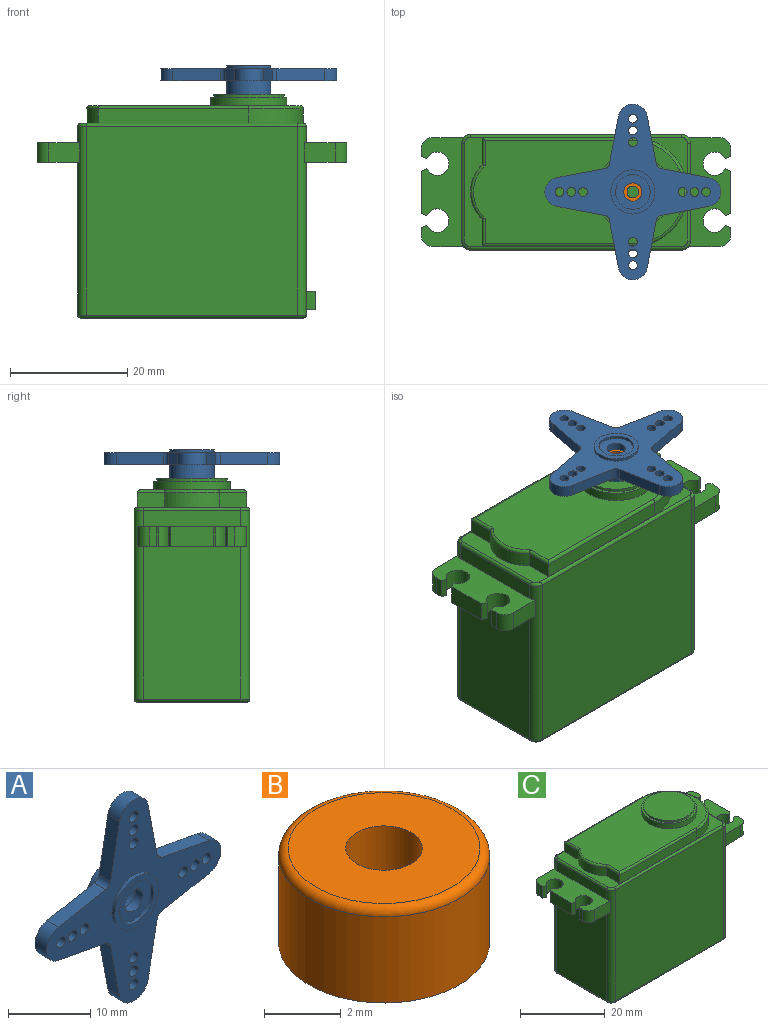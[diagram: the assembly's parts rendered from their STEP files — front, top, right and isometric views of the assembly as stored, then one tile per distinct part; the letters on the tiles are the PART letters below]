
ASSEMBLY  parts=3 mates=2
PART A: 39 faces, bbox 30x4.9x30 mm
  f0: plane 8.17x2mm, normal (-0.18,0,0.98), area 16.6mm2, adj f1,f24,f25,f38
  f1: cylinder r=2.5mm len=4.91mm, axis (0,1,0), area 13.8mm2, adj f0,f2,f24,f25
  f2: plane 8.17x2mm, normal (-0.18,0,-0.98), area 16.6mm2, adj f1,f24,f25,f35
  f3: plane 8.17x2mm, normal (-0.98,0,-0.18), area 16.6mm2, adj f4,f24,f25,f35
  f4: cylinder r=2.5mm len=4.91mm, axis (0,1,0), area 13.8mm2, adj f3,f5,f24,f25
  f5: plane 8.17x2mm, normal (0.98,0,-0.18), area 16.6mm2, adj f4,f24,f25,f36
  f6: plane 8.17x2mm, normal (0.18,0,-0.98), area 16.6mm2, adj f7,f24,f25,f36
  f7: cylinder r=2.5mm len=4.91mm, axis (0,1,0), area 13.8mm2, adj f6,f8,f24,f25
  f8: plane 8.17x2mm, normal (0.18,0,0.98), area 16.6mm2, adj f7,f24,f25,f37
  f9: plane 8.17x2mm, normal (0.98,0,0.18), area 16.6mm2, adj f10,f24,f25,f37
  f10: cylinder r=2.5mm len=4.91mm, axis (0,1,0), area 13.8mm2, adj f9,f23,f24,f25
  f11: cylinder r=0.75mm len=2mm, axis (0,1,0), area 9.4mm2, adj f24,f25
  f12: cylinder r=0.75mm len=2mm, axis (0,1,0), area 9.4mm2, adj f24,f25
  f13: cylinder r=0.75mm len=2mm, axis (0,1,0), area 9.4mm2, adj f24,f25
  f14: cylinder r=0.75mm len=2mm, axis (0,1,0), area 9.4mm2, adj f24,f25
  f15: cylinder r=0.75mm len=2mm, axis (0,1,0), area 9.4mm2, adj f24,f25
  f16: cylinder r=0.75mm len=2mm, axis (0,1,0), area 9.4mm2, adj f24,f25
  f17: cylinder r=0.75mm len=2mm, axis (0,1,0), area 9.4mm2, adj f24,f25
  f18: cylinder r=0.75mm len=2mm, axis (0,1,0), area 9.4mm2, adj f24,f25
  f19: cylinder r=0.75mm len=2mm, axis (0,1,0), area 9.4mm2, adj f24,f25
  f20: cylinder r=0.75mm len=2mm, axis (0,1,0), area 9.4mm2, adj f24,f25
  f21: cylinder r=0.75mm len=2mm, axis (0,1,0), area 9.4mm2, adj f24,f25
  f22: cylinder r=0.75mm len=2mm, axis (0,1,0), area 9.4mm2, adj f24,f25
  f23: plane 8.17x2mm, normal (-0.98,0,0.18), area 16.6mm2, adj f10,f24,f25,f38
  f24: plane 30x30mm, normal (0,-1,0), area 265.3mm2, adj f0,f1,f2,f3,f4,f5,f6,f7
  f25: plane 30x30mm, normal (0,1,0), area 265.3mm2, adj f0,f1,f2,f3,f4,f5,f6,f7
  f26: cylinder r=3.76mm len=7.52mm, axis (0,1,0), area 11.8mm2, adj f24,f27
  f27: plane 7.52x7.52mm, normal (0,-1,0), area 17.1mm2, adj f26,f32
  f28: cylinder r=3.76mm len=7.52mm, axis (0,-1,0), area 56.7mm2, adj f25,f29
  f29: plane 7.52x7.52mm, normal (0,1,0), area 17.1mm2, adj f28,f30
  f30: cylinder r=2.95mm len=5.9mm, axis (0,1,0), area 57.5mm2, adj f29,f31
  f31: plane 5.9x5.9mm, normal (0,1,0), area 19.8mm2, adj f30,f34
  f32: cylinder r=2.95mm len=5.9mm, axis (0,-1,0), area 9.3mm2, adj f27,f33
  f33: plane 5.9x5.9mm, normal (0,-1,0), area 19.8mm2, adj f32,f34
  f34: cylinder r=1.55mm len=3.1mm, axis (0,-1,0), area 12.7mm2, adj f31,f33
  f35: cylinder r=1mm len=2mm, axis (0,1,0), area 2.4mm2, adj f2,f3,f24,f25
  f36: cylinder r=1mm len=2mm, axis (0,1,0), area 2.4mm2, adj f5,f6,f24,f25
  f37: cylinder r=1mm len=2mm, axis (0,1,0), area 2.4mm2, adj f8,f9,f24,f25
  f38: cylinder r=1mm len=2mm, axis (0,1,0), area 2.4mm2, adj f0,f23,f24,f25
PART B: 5 faces, bbox 6x6x3 mm
  f0: cylinder r=1mm len=3mm, axis (0,0,-1), area 18.8mm2, adj f2,f3
  f1: cylinder r=2.75mm len=5.5mm, axis (0,0,-1), area 47.5mm2, adj f3,f4
  f2: plane 5x5mm, normal (0,0,1), area 16.5mm2, adj f0,f4
  f3: plane 5.5x5.5mm, normal (0,0,-1), area 20.6mm2, adj f0,f1
  f4: torus R=2.5mm, axis (0,0,1), area 6.6mm2, adj f1,f2
PART C: 80 faces, bbox 52.9x20.1x38.2 mm
  f0: plane 16.7x2.8mm, normal (-1,0,0), area 46.8mm2, adj f17,f52,f53,f78
  f1: plane 26.06x16.7mm, normal (1,0,0), area 415mm2, adj f6,f33,f34,f35,f36,f50,f51,f66
  f2: plane 3.34x1.2mm, normal (1,0,0), area 4mm2, adj f6,f16,f47,f55
  f3: plane 7.2x3.34mm, normal (1,0,0), area 24mm2, adj f6,f16,f44,f48
  f4: plane 7.2x3.34mm, normal (-1,0,0), area 24mm2, adj f17,f18,f39,f43
  f5: plane 3.34x1.2mm, normal (-1,0,0), area 4mm2, adj f17,f18,f40,f57
  f6: plane 18.6x7.27mm, normal (0,0,-1), area 98.7mm2, adj f1,f2,f3,f13,f14,f15,f44,f45
  f7: plane 38x18.7mm, normal (0,0,1), area 82.9mm2, adj f22,f23,f24,f25,f26,f27,f72,f73
  f8: plane 26.06x16.7mm, normal (-1,0,0), area 435.2mm2, adj f18,f52,f53,f69
  f9: plane 38x18.7mm, normal (0,0,-1), area 709.7mm2, adj f64,f65,f66,f67,f68,f69,f70,f71
  f10: plane 16.7x2.8mm, normal (1,0,0), area 46.8mm2, adj f16,f50,f51,f73
  f11: plane 36x32.2mm, normal (0,-1,0), area 1159.2mm2, adj f50,f52,f65,f74
  f12: plane 36x32.2mm, normal (0,1,0), area 1159.2mm2, adj f51,f53,f70,f77
  f13: plane 3.34x1.2mm, normal (1,0,0), area 4mm2, adj f6,f16,f45,f54
  f14: plane 5.27x3.34mm, normal (0,-1,0), area 17.6mm2, adj f6,f16,f50,f55
  f15: plane 5.27x3.34mm, normal (0,1,0), area 17.6mm2, adj f6,f16,f51,f54
  f16: plane 18.6x7.27mm, normal (0,0,1), area 98.7mm2, adj f2,f3,f10,f13,f14,f15,f44,f45
  f17: plane 18.6x7.27mm, normal (0,0,1), area 98.7mm2, adj f0,f4,f5,f19,f20,f21,f38,f39
  f18: plane 18.6x7.27mm, normal (0,0,-1), area 98.7mm2, adj f4,f5,f8,f19,f20,f21,f38,f39
  f19: plane 5.27x3.34mm, normal (0,-1,0), area 17.6mm2, adj f17,f18,f52,f57
  f20: plane 5.27x3.34mm, normal (0,1,0), area 17.6mm2, adj f17,f18,f53,f56
  f21: plane 3.34x1.2mm, normal (-1,0,0), area 4mm2, adj f17,f18,f42,f56
  f22: cylinder r=6.5mm len=9.38mm, axis (0,0,-1), area 26.2mm2, adj f7,f23,f27,f58
  f23: plane 4.61x2.5mm, normal (-1,0,0), area 11.5mm2, adj f7,f22,f24,f59
  f24: plane 25.7x2.5mm, normal (0,-1,0), area 64.3mm2, adj f7,f23,f25,f61
  f25: cylinder r=9.3mm len=18.6mm, axis (0,0,-1), area 73mm2, adj f7,f24,f26,f63
  f26: plane 25.7x2.5mm, normal (0,1,0), area 64.3mm2, adj f7,f25,f27,f62
  f27: plane 4.61x2.5mm, normal (-1,0,0), area 11.5mm2, adj f7,f22,f26,f60
  f28: plane 36x17.6mm, normal (0,0,1), area 444.8mm2, adj f29,f58,f59,f60,f61,f62,f63
  f29: cylinder r=6.5mm len=13mm, axis (0,0,-1), area 61.3mm2, adj f28,f30
  f30: plane 13x13mm, normal (0,0,1), area 19.6mm2, adj f29,f31
  f31: cylinder r=6mm len=12mm, axis (0,0,-1), area 18.8mm2, adj f30,f32
  f32: plane 12x12mm, normal (0,0,1), area 113.1mm2, adj f31
  f33: plane 6.4x1.5mm, normal (0,0,1), area 9.6mm2, adj f1,f34,f36,f37
  f34: plane 3.15x1.5mm, normal (0,-1,0), area 4.7mm2, adj f1,f33,f35,f37
  f35: plane 6.4x1.5mm, normal (0,0,-1), area 9.6mm2, adj f1,f34,f36,f37
  f36: plane 3.15x1.5mm, normal (0,1,0), area 4.7mm2, adj f1,f33,f35,f37
  f37: plane 6.4x3.15mm, normal (1,0,0), area 20.2mm2, adj f33,f34,f35,f36
  f38: cylinder r=2mm len=4mm, axis (0,0,1), area 36.3mm2, adj f17,f18,f39,f40
  f39: plane 3.34x0.94mm, normal (-0.41,-0.91,0), area 3.4mm2, adj f4,f17,f18,f38
  f40: plane 3.34x0.94mm, normal (-0.41,0.91,0), area 3.4mm2, adj f5,f17,f18,f38
  f41: cylinder r=2mm len=4mm, axis (0,0,1), area 36.3mm2, adj f17,f18,f42,f43
  f42: plane 3.34x0.94mm, normal (-0.41,-0.91,0), area 3.4mm2, adj f17,f18,f21,f41
  f43: plane 3.34x0.94mm, normal (-0.41,0.91,0), area 3.4mm2, adj f4,f17,f18,f41
  f44: plane 3.34x0.94mm, normal (0.41,0.91,0), area 3.4mm2, adj f3,f6,f16,f46
  f45: plane 3.34x0.94mm, normal (0.41,-0.91,0), area 3.4mm2, adj f6,f13,f16,f46
  f46: cylinder r=2mm len=4mm, axis (0,0,1), area 36.3mm2, adj f6,f16,f44,f45
  f47: plane 3.34x0.94mm, normal (0.41,0.91,0), area 3.4mm2, adj f2,f6,f16,f49
  f48: plane 3.34x0.94mm, normal (0.41,-0.91,0), area 3.4mm2, adj f3,f6,f16,f49
  f49: cylinder r=2mm len=4mm, axis (0,0,1), area 36.3mm2, adj f6,f16,f47,f48
  f50: cylinder r=1.5mm len=32.2mm, axis (0,0,-1), area 72.4mm2, adj f1,f6,f10,f11,f14,f16,f64,f72
  f51: cylinder r=1.5mm len=32.2mm, axis (0,0,1), area 72.4mm2, adj f1,f6,f10,f12,f15,f16,f68,f75
  f52: cylinder r=1.5mm len=32.2mm, axis (0,0,1), area 72.4mm2, adj f0,f8,f11,f17,f18,f19,f67,f76
  f53: cylinder r=1.5mm len=32.2mm, axis (0,0,-1), area 72.4mm2, adj f0,f8,f12,f17,f18,f20,f71,f79
  f54: cylinder r=2mm len=3.34mm, axis (0,0,1), area 10.5mm2, adj f6,f13,f15,f16
  f55: cylinder r=2mm len=3.34mm, axis (0,0,-1), area 10.5mm2, adj f2,f6,f14,f16
  f56: cylinder r=2mm len=3.34mm, axis (0,0,-1), area 10.5mm2, adj f17,f18,f20,f21
  f57: cylinder r=2mm len=3.34mm, axis (0,0,1), area 10.5mm2, adj f5,f17,f18,f19
  f58: torus R=6mm, axis (0,0,1), area 8.1mm2, adj f22,f28,f59,f60
  f59: cylinder r=0.5mm len=4.83mm, axis (0,1,0), area 3.5mm2, adj f23,f28,f58,f61
  f60: cylinder r=0.5mm len=4.83mm, axis (0,1,0), area 3.5mm2, adj f27,f28,f58,f62
  f61: cylinder r=0.5mm len=25.7mm, axis (-1,0,0), area 20mm2, adj f24,f28,f59,f63
  f62: cylinder r=0.5mm len=25.7mm, axis (1,0,0), area 20mm2, adj f26,f28,f60,f63
  f63: torus R=8.8mm, axis (0,0,1), area 22.5mm2, adj f25,f28,f61,f62
  f64: torus R=1mm, axis (0,0,1), area 1.6mm2, adj f9,f50,f65,f66
  f65: cylinder r=0.5mm len=36mm, axis (-1,0,0), area 28.3mm2, adj f9,f11,f64,f67
  f66: cylinder r=0.5mm len=16.7mm, axis (0,-1,0), area 13.1mm2, adj f1,f9,f64,f68
  f67: torus R=1mm, axis (0,0,1), area 1.6mm2, adj f9,f52,f65,f69
  f68: torus R=1mm, axis (0,0,1), area 1.6mm2, adj f9,f51,f66,f70
  f69: cylinder r=0.5mm len=16.7mm, axis (0,1,0), area 13.1mm2, adj f8,f9,f67,f71
  f70: cylinder r=0.5mm len=36mm, axis (1,0,0), area 28.3mm2, adj f9,f12,f68,f71
  f71: torus R=1mm, axis (0,0,1), area 1.6mm2, adj f9,f53,f69,f70
  f72: torus R=1mm, axis (0,0,1), area 1.6mm2, adj f7,f50,f73,f74
  f73: cylinder r=0.5mm len=16.7mm, axis (0,1,0), area 13.1mm2, adj f7,f10,f72,f75
  f74: cylinder r=0.5mm len=36mm, axis (1,0,0), area 28.3mm2, adj f7,f11,f72,f76
  f75: torus R=1mm, axis (0,0,1), area 1.6mm2, adj f7,f51,f73,f77
  f76: torus R=1mm, axis (0,0,1), area 1.6mm2, adj f7,f52,f74,f78
  f77: cylinder r=0.5mm len=36mm, axis (-1,0,0), area 28.3mm2, adj f7,f12,f75,f79
  f78: cylinder r=0.5mm len=16.7mm, axis (0,-1,0), area 13.1mm2, adj f0,f7,f76,f79
  f79: torus R=1mm, axis (0,0,1), area 1.6mm2, adj f7,f53,f77,f78
PLACE A rot(axis=(-1,0,0),90deg) t=(9.64,-0.31,20.98)mm
PLACE B t=(9.64,-0.31,7.04)mm
PLACE C t=(9.64,-0.31,7.04)mm
MATE fastened A.f34 <-> B.f0  axis (0,0,-1) through (9.64,-0.31,21.68)mm
MATE revolute B.f0 <-> C.f31  axis (0,0,-1) through (9.64,-0.31,18.68)mm
